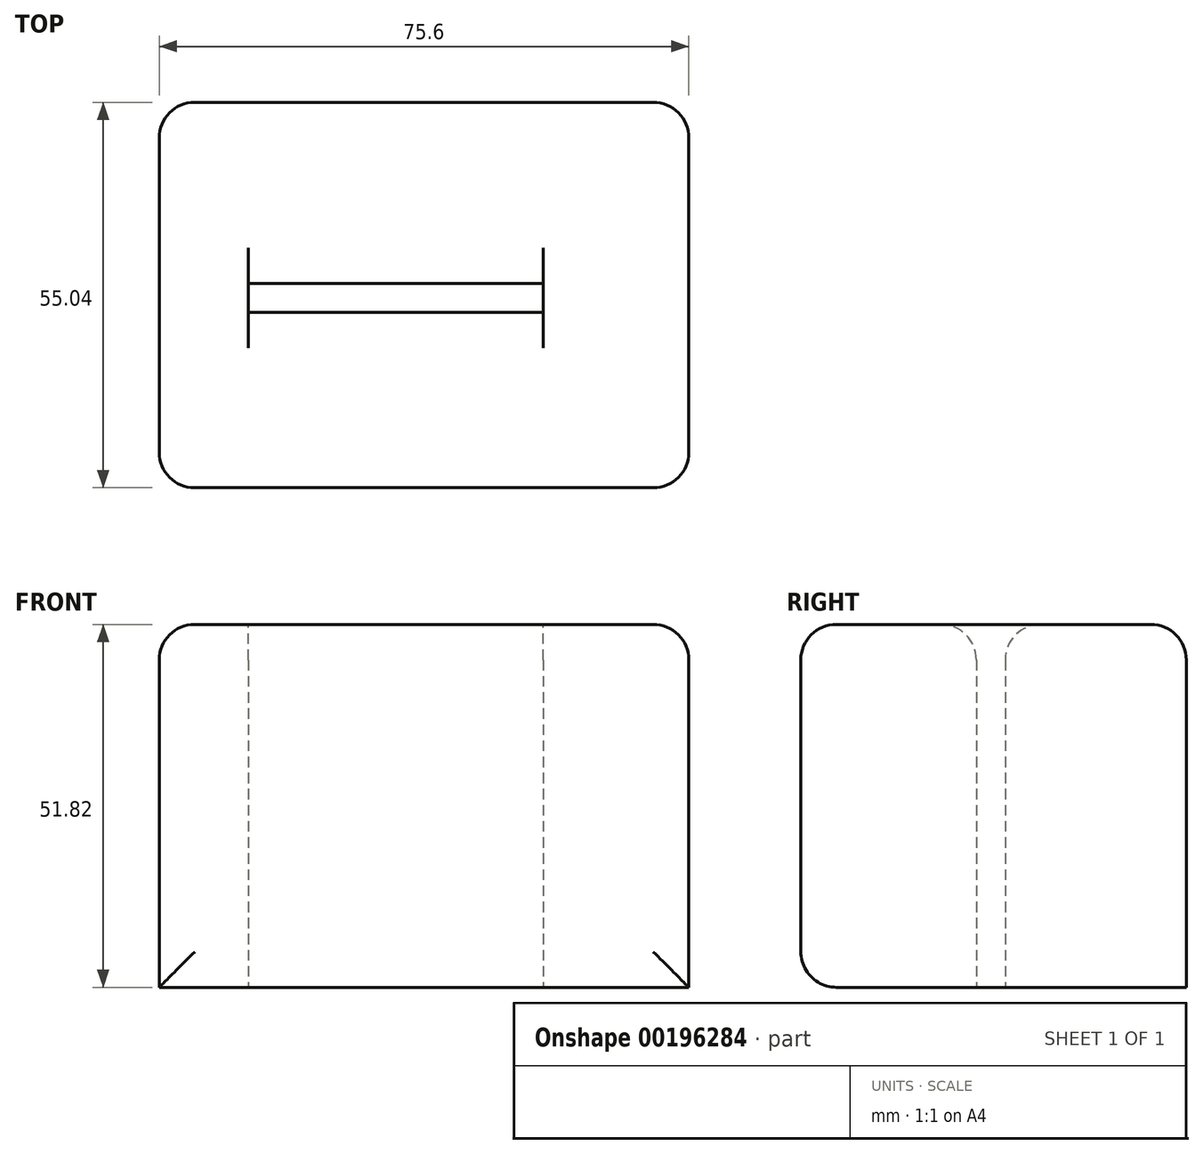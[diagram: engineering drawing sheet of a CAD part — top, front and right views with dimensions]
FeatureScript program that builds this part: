
annotation { "Feature Type Name" : "Feature", "Feature Type Description" : "" }
export const myFeature = defineFeature(function(context is Context, id is Id, definition is map)
    precondition{}
    {
        {
            var Q0;
            Q0=qCreatedBy(makeId("Top.planeOp"),FACE);
            var sketch = newSketch(context, id + "F0", { "sketchPlane" : qUnion([Q0])});
            skLineSegment(sketch, "E0.bottom", {"start": v(-29.38, 15.38) * mm, "end": v(46.22, 15.38) * mm});
            skLineSegment(sketch, "E0.top", {"start": v(-29.38, -39.66) * mm, "end": v(46.22, -39.66) * mm});
            skLineSegment(sketch, "E0.left", {"start": v(-29.38, 15.38) * mm, "end": v(-29.38, -39.66) * mm});
            skLineSegment(sketch, "E0.right", {"start": v(46.22, 15.38) * mm, "end": v(46.22, -39.66) * mm});
            skLineSegment(sketch, "E1.bottom", {"start": v(-7.25, -10.48) * mm, "end": v(25.46, -10.48) * mm});
            skLineSegment(sketch, "E1.top", {"start": v(-7.25, -14.6) * mm, "end": v(25.46, -14.6) * mm});
            skLineSegment(sketch, "E1.left", {"start": v(-7.25, -10.48) * mm, "end": v(-7.25, -14.6) * mm});
            skLineSegment(sketch, "E1.right", {"start": v(25.46, -10.48) * mm, "end": v(25.46, -14.6) * mm});
            skLineSegment(sketch, "E2.bottom", {"start": v(-7.25, -14.6) * mm, "end": v(-12.34, -14.6) * mm});
            skLineSegment(sketch, "E2.top", {"start": v(-7.25, -14.6) * mm, "end": v(-12.34, -14.6) * mm});
            skLineSegment(sketch, "E2.left", {"start": v(-7.25, -14.6) * mm, "end": v(-7.25, -14.6) * mm});
            skLineSegment(sketch, "E2.right", {"start": v(-12.34, -14.6) * mm, "end": v(-12.34, -14.6) * mm});
            skLineSegment(sketch, "E3.bottom", {"start": v(-16.65, -14.6) * mm, "end": v(-12.34, -14.6) * mm});
            skLineSegment(sketch, "E3.top", {"start": v(-16.65, -14.6) * mm, "end": v(-12.34, -14.6) * mm});
            skLineSegment(sketch, "E3.left", {"start": v(-16.65, -14.6) * mm, "end": v(-16.65, -14.6) * mm});
            skLineSegment(sketch, "E4.top", {"start": v(-16.65, -11.26) * mm, "end": v(-16.65, -11.26) * mm});
            skLineSegment(sketch, "E4.left", {"start": v(-16.65, -14.6) * mm, "end": v(-16.65, -11.26) * mm});
            skLineSegment(sketch, "E4.right", {"start": v(-16.65, -14.6) * mm, "end": v(-16.65, -11.26) * mm});
            skLineSegment(sketch, "E5.bottom", {"start": v(-7.25, -10.48) * mm, "end": v(-16.65, -10.48) * mm});
            skLineSegment(sketch, "E5.top", {"start": v(-7.25, -11.26) * mm, "end": v(-16.65, -11.26) * mm});
            skLineSegment(sketch, "E5.left", {"start": v(-7.25, -10.48) * mm, "end": v(-7.25, -11.26) * mm});
            skLineSegment(sketch, "E5.right", {"start": v(-16.65, -10.48) * mm, "end": v(-16.65, -11.26) * mm});
            skSolve(sketch);
        }
        {
            var Q0;
            Q0=makeQuery(id+"F0.imprint","IMPRINT",FACE,{"disambiguationData":[TD([[makeQuery(id+"F0.imprint","IMPRINT",EDGE,{"derivedFrom":sQuery(id+"F0.wireOp",EDGE,"E0.bottom")}),-1.0]])]});
            extrude(context, id + "F1", {"entities" : qUnion([Q0]), "depth" : 51.82 * mm});
        }
        {
            var Q0;
            Q0=makeQuery(id+"F1.opExtrude","CAP_EDGE",EDGE,{"disambiguationData":[OSD([sQuery(id+"F0.wireOp",EDGE,"E1.top"),sQuery(id+"F0.wireOp",EDGE,"E2.top"),sQuery(id+"F0.wireOp",EDGE,"E3.top")])],"isStart":false});
            fillet(context, id + "F2", {"entities" : qUnion([Q0]), "radius" : 5.08 * mm, "tangentPropagation" : true, "allowEdgeOverflow" : false});
        }
        {
            var Q0;
            Q0=makeQuery(id+"F1.opExtrude","CAP_EDGE",EDGE,{"disambiguationData":[OSD([sQuery(id+"F0.wireOp",EDGE,"E0.bottom")])],"isStart":false});
            var Q1;
            Q1=makeQuery(id+"F1.opExtrude","CAP_EDGE",EDGE,{"disambiguationData":[OSD([sQuery(id+"F0.wireOp",EDGE,"E0.top")])],"isStart":false});
            var Q2;
            Q2=makeQuery(id+"F1.opExtrude","CAP_EDGE",EDGE,{"disambiguationData":[OSD([sQuery(id+"F0.wireOp",EDGE,"E0.right")])],"isStart":false});
            var Q3;
            Q3=makeQuery(id+"F1.opExtrude","CAP_EDGE",EDGE,{"disambiguationData":[OSD([sQuery(id+"F0.wireOp",EDGE,"E0.left")])],"isStart":false});
            var Q4;
            Q4=makeQuery(id+"F1.opExtrude","CAP_EDGE",EDGE,{"disambiguationData":[OSD([sQuery(id+"F0.wireOp",EDGE,"E1.bottom"),sQuery(id+"F0.wireOp",EDGE,"E5.bottom")])],"isStart":false});
            var Q5;
            Q5=makeQuery(id+"F1.opExtrude","SWEPT_FACE",FACE,{"disambiguationData":[OSD([sQuery(id+"F0.wireOp",EDGE,"E0.top")])]});
            var Q6;
            Q6=makeQuery(id+"F1.opExtrude","SWEPT_EDGE",EDGE,{"disambiguationData":[OSD([sQuery(id+"F0.wireOp",EDGE,"E0.bottom"),sQuery(id+"F0.wireOp",EDGE,"E0.right")])]});
            var Q7;
            Q7=makeQuery(id+"F1.opExtrude","SWEPT_EDGE",EDGE,{"disambiguationData":[OSD([sQuery(id+"F0.wireOp",EDGE,"E0.bottom"),sQuery(id+"F0.wireOp",EDGE,"E0.left")])]});
            fillet(context, id + "F3", {"entities" : qUnion([Q0, Q1, Q2, Q3, Q4, Q5, Q6, Q7]), "radius" : 5.08 * mm, "tangentPropagation" : true, "allowEdgeOverflow" : false});
        }
    });
